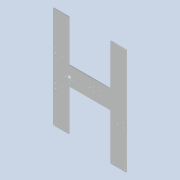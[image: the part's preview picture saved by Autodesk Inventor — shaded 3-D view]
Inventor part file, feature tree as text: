
AUTODESK INVENTOR PART (.ipt)
format: ipt  version: 2020 (Build 240168000, 168)  size: 233,472 bytes
history: native  units: mm
features: sketch x5, extrude x4, reference x4, other x4, hole x1
ambient origin geometry x8: Origin, YZ Plane, XZ Plane, XY Plane, X Axis, Y Axis, Z Axis, Center Point
bodies: Solid1 (feature_tree)
feature tree (18):
  extrude  "Extrusion1"  Depth=317.0mm
  extrude  "Extrusion3"  Depth=5.0mm
  extrude  "Extrusion5"  Depth=4.0mm TaperAngle=0.0deg
  hole  "Hole1"  [1 undecoded]
  extrude  "Extrusion6"  Depth=20.0mm
  sketch  "Sketch1"  dims[d0=440.0mm d1=317.0mm]
  sketch  "Sketch3"  dims[d3=5.0mm d4=5.0mm]
  sketch  "Sketch5"  dims[d5=4.0mm d6=4.0mm d7=0.0mm]
  sketch  "Sketch6"  dims[d11=180.0mm d12=80.0mm]
  sketch  "Sketch7"  dims[d13=0.0mm d14=0.0mm d21=20.0mm d22=5.0mm d24=50.0mm d25=0.0mm d26=0.0mm d27=5.0mm d28=6.0mm d29=9.0mm d30=5.0mm d31=90.0deg d32=8.0mm d33=20.594885mm d34=5.0mm d35=4.0mm d37=8.0mm d38=12.0mm d39=15.0mm d40=35.0mm d41=6.0mm d42=12.0mm d43=15.0mm d44=5.0mm d45=0.0mm d46=0.0mm d47=5.5mm]
  reference  "Reference1"
  reference  "Reference2"
  reference  "Reference3"
  reference  "Reference4"
  parser-record x1  (decoder bookkeeping rows leaked as tree rows — omitted from the tree; the rows remain in map.json)
  other  "0008-10-03 YAxis.iam"
  other  "0008-10-1026 wire chain Y.ipt:43"
  other  "0008-20-1007 HEATING BED.ipt:36"
note: 1 required parameter value undecoded (feature->parameter linkage not recoverable at this tier; creation-order binding heuristic only, values carry confidence <= 0.55)
note: 1 file-system path scrubbed to <path> (originals preserved in map.json)
